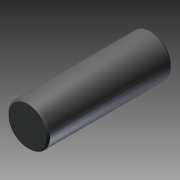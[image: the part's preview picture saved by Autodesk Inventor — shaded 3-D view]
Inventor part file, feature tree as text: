
AUTODESK INVENTOR PART (.ipt)
format: ipt  version: 2011 SP1 (Build 150282100, 282)  size: 90,112 bytes
history: native  units: in
note: dims shown in document units (in); Inventor stores cm internally (conversion verified against a paired STEP export)
features: other x35, revolve x1, sketch x1
ambient origin geometry x8: Origin, YZ Plane, XZ Plane, XY Plane, X Axis, Y Axis, Z Axis, Center Point
bodies: Solid1 (feature_tree)
feature tree (37):
  revolve  "Revolution1"  [1 undecoded]
  other  "dia1_XY"
  other  "dia1_YZ"
  other  "dia1_ZX"
  other  "dia1_X"
  other  "dia1_Y"
  other  "dia1_Z"
  other  "dia1_Center"
  other  "dia2_XY"
  other  "dia2_YZ"
  other  "dia2_ZX"
  other  "dia2_X"
  other  "dia2_Y"
  other  "dia2_Z"
  other  "dia2_Center"
  other  "pin_XY"
  other  "pin_YZ"
  other  "pin_ZX"
  other  "pin_X"
  other  "pin_Y"
  other  "pin_Z"
  other  "pin_Center"
  other  "pin1_XY"
  other  "pin1_YZ"
  other  "pin1_ZX"
  other  "pin1_X"
  other  "pin1_Y"
  other  "pin1_Z"
  other  "pin1_Center"
  other  "pin2_XY"
  other  "pin2_YZ"
  other  "pin2_ZX"
  other  "pin2_X"
  other  "pin2_Y"
  other  "pin2_Z"
  other  "pin2_Center"
  sketch  "Sketch_1"  dims[d0=360.0deg]
note: 1 required parameter value undecoded (feature->parameter linkage not recoverable at this tier; creation-order binding heuristic only, values carry confidence <= 0.55)
